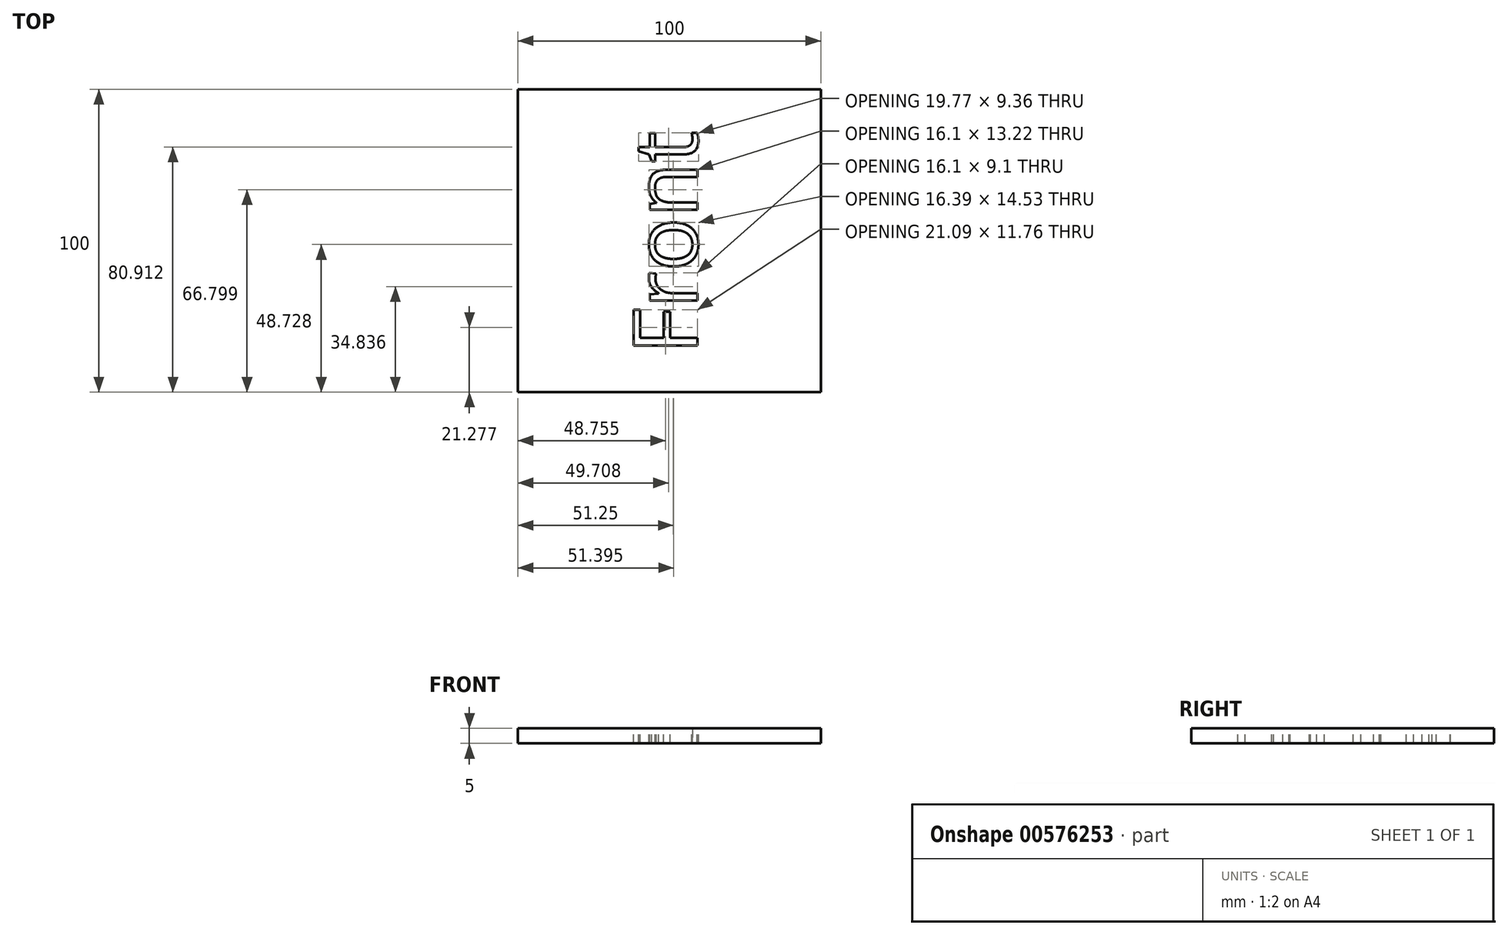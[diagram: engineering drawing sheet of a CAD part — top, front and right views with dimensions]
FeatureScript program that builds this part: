
annotation { "Feature Type Name" : "Feature", "Feature Type Description" : "" }
export const myFeature = defineFeature(function(context is Context, id is Id, definition is map)
    precondition{}
    {
        {
            var Q0;
            Q0=qCreatedBy(makeId("Top.planeOp"),FACE);
            var sketch = newSketch(context, id + "F0", { "sketchPlane" : qUnion([Q0])});
            skLineSegment(sketch, "E0.bottom", {"start": v(50, 50) * mm, "end": v(-50, 50) * mm});
            skLineSegment(sketch, "E0.top", {"start": v(50, -50) * mm, "end": v(-50, -50) * mm});
            skLineSegment(sketch, "E0.left", {"start": v(50, 50) * mm, "end": v(50, -50) * mm});
            skLineSegment(sketch, "E0.right", {"start": v(-50, 50) * mm, "end": v(-50, -50) * mm});
            skPoint(sketch, "E0.middle", {"position": v(0, 0) * mm});
            skSolve(sketch);
        }
        {
            var Q0;
            Q0 = qSketchRegion(id + "F0", true);
            extrude(context, id + "F1", {"entities" : qUnion([Q0]), "depth" : 5 * mm, "offsetDistance" : 25 * mm});
        }
        {
            var Q0;
            Q0=makeQuery(id+"F1.opExtrude","CAP_FACE",FACE,{"disambiguationData":[OSD([sQuery(id+"F0.wireOp",EDGE,"E0.bottom"),sQuery(id+"F0.wireOp",EDGE,"E0.top"),sQuery(id+"F0.wireOp",EDGE,"E0.left"),sQuery(id+"F0.wireOp",EDGE,"E0.right")])],"isStart":false});
            var sketch = newSketch(context, id + "F2", { "sketchPlane" : qUnion([Q0])});
            skText(sketch, "E1", { "text": "Front\n", "fontName": "OpenSans-Regular.ttf"});
            const initialGuessF2  = {"E1": [0.0093, -0.0375, 0, 1, 0.02127]};
            skSetInitialGuess(sketch, initialGuessF2);
            skSolve(sketch);
        }
        {
            var Q0;
            Q0 = qSketchRegion(id + "F2", true);
            extrude(context, id + "F3", {"entities" : qUnion([Q0]), "operationType" : NewBodyOperationType.REMOVE, "oppositeDirection" : true, "depth" : 5 * mm, "offsetDistance" : 25 * mm});
        }
    });
